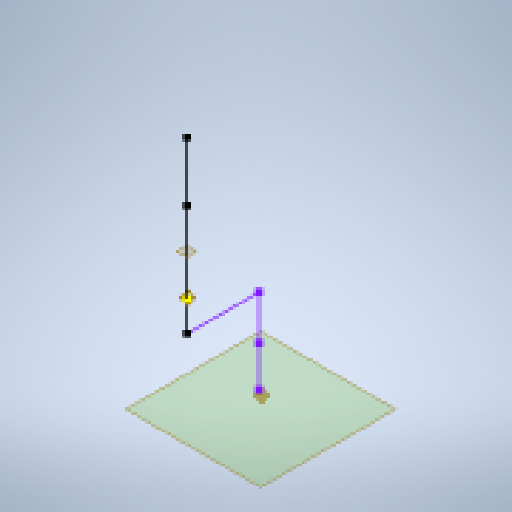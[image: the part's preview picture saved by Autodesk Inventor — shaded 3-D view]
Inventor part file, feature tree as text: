
AUTODESK INVENTOR PART (.ipt)
format: ipt  version: 2025 (Build 290162000, 162)  size: 163,840 bytes
history: native  units: in
note: dims shown in document units (in); Inventor stores cm internally (conversion verified against a paired STEP export)
features: plane x1, other x1, sketch x1
ambient origin geometry x8: Origin, YZ Plane, XZ Plane, XY Plane, X Axis, Y Axis, Z Axis, Center Point
feature tree (3):
  plane  "Work Plane2"
  other  "Work Point2"
  sketch  "3D Sketch1"
